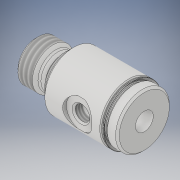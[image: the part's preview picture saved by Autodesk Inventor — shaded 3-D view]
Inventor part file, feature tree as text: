
AUTODESK INVENTOR PART (.ipt)
format: ipt  version: 2019 (Build 230136000, 136)  size: 286,208 bytes
history: native  units: in
note: dims shown in document units (in); Inventor stores cm internally (conversion verified against a paired STEP export)
features: other x119, sketch x5, revolve x4, thread x2, hole x1
ambient origin geometry x8: Origin, YZ Plane, XZ Plane, XY Plane, X Axis, Y Axis, Z Axis, Center Point
bodies: Solid1 (feature_tree)
feature tree (131):
  revolve  "Revolution1"  [1 undecoded]
  thread  "Thread1"  [1 undecoded]
  revolve  "Revolution2"  Angle=360.0deg
  hole  "Hole1"  [1 undecoded]
  revolve  "Revolution3"  [1 undecoded]
  thread  "Thread2"  [1 undecoded]
  revolve  "Revolution4"  [1 undecoded]
  other  "dp1_XY"
  other  "dp1_YZ"
  other  "dp1_ZX"
  other  "dp1_X"
  other  "dp1_Y"
  other  "dp1_Z"
  other  "dp1_Center"
  other  "dp2_XY"
  other  "dp2_YZ"
  other  "dp2_ZX"
  other  "dp2_X"
  other  "dp2_Y"
  other  "dp2_Z"
  other  "dp2_Center"
  other  "hh_XY"
  other  "hh_YZ"
  other  "hh_ZX"
  other  "hh_X"
  other  "hh_Y"
  other  "hh_Z"
  other  "hh_Center"
  other  "port_XY"
  other  "port_YZ"
  other  "port_ZX"
  other  "port_X"
  other  "port_Y"
  other  "port_Z"
  other  "port_Center"
  other  "rod_guide_XY"
  other  "rod_guide_YZ"
  other  "rod_guide_ZX"
  other  "rod_guide_X"
  other  "rod_guide_Y"
  other  "rod_guide_Z"
  other  "rod_guide_Center"
  other  "s1_XY"
  other  "s1_YZ"
  other  "s1_ZX"
  other  "s1_X"
  other  "s1_Y"
  other  "s1_Z"
  other  "s1_Center"
  other  "s2_XY"
  other  "s2_YZ"
  other  "s2_ZX"
  other  "s2_X"
  other  "s2_Y"
  other  "s2_Z"
  other  "s2_Center"
  other  "t1_XY"
  other  "t1_YZ"
  other  "t1_ZX"
  other  "t1_X"
  other  "t1_Y"
  other  "t1_Z"
  other  "t1_Center"
  other  "t111_XY"
  other  "t111_YZ"
  other  "t111_ZX"
  other  "t111_X"
  other  "t111_Y"
  other  "t111_Z"
  other  "t111_Center"
  other  "to_foot_bracket_XY"
  other  "to_foot_bracket_YZ"
  other  "to_foot_bracket_ZX"
  other  "to_foot_bracket_X"
  other  "to_foot_bracket_Y"
  other  "to_foot_bracket_Z"
  other  "to_foot_bracket_Center"
  other  "to_nut_XY"
  other  "to_nut_YZ"
  other  "to_nut_ZX"
  other  "to_nut_X"
  other  "to_nut_Y"
  other  "to_nut_Z"
  other  "to_nut_Center"
  other  "to_rod_XY"
  other  "to_rod_YZ"
  other  "to_rod_ZX"
  other  "to_rod_X"
  other  "to_rod_Y"
  other  "to_rod_Z"
  other  "to_rod_Center"
  other  "to_screw_XY"
  other  "to_screw_YZ"
  other  "to_screw_ZX"
  other  "to_screw_X"
  other  "to_screw_Y"
  other  "to_screw_Z"
  other  "to_screw_Center"
  other  "to_trunnion_brackets_XY"
  other  "to_trunnion_brackets_YZ"
  other  "to_trunnion_brackets_ZX"
  other  "to_trunnion_brackets_X"
  other  "to_trunnion_brackets_Y"
  other  "to_trunnion_brackets_Z"
  other  "to_trunnion_brackets_Center"
  other  "to_trunnion_brackets1_XY"
  other  "to_trunnion_brackets1_YZ"
  other  "to_trunnion_brackets1_ZX"
  other  "to_trunnion_brackets1_X"
  other  "to_trunnion_brackets1_Y"
  other  "to_trunnion_brackets1_Z"
  other  "to_trunnion_brackets1_Center"
  other  "to_trunnion_brackets2_XY"
  other  "to_trunnion_brackets2_YZ"
  other  "to_trunnion_brackets2_ZX"
  other  "to_trunnion_brackets2_X"
  other  "to_trunnion_brackets2_Y"
  other  "to_trunnion_brackets2_Z"
  other  "to_trunnion_brackets2_Center"
  other  "to_tube_XY"
  other  "to_tube_YZ"
  other  "to_tube_ZX"
  other  "to_tube_X"
  other  "to_tube_Y"
  other  "to_tube_Z"
  other  "to_tube_Center"
  sketch  "Sketch_2"  dims[d0=360.0deg d1=0.1537in d2=0.0in d3=360.0deg]
  sketch  "Sketch_3"  dims[d4=0.19in d5=0.75in d6=0.23in d7=0.25in d8=90.0deg d9=1.156in d10=0.0in d11=360.0deg]
  sketch  "Sketch3"  dims[d12=0.0786in d13=0.0in d14=360.0deg]
  sketch  "Sketch_12"  dims[d15=0.0in d16=0.0in d17=0.0in d18=0.0in d19=0.0in d20=0.0in]
  sketch  "Sketch_47"
note: 6 required parameter values undecoded (feature->parameter linkage not recoverable at this tier; creation-order binding heuristic only, values carry confidence <= 0.55)